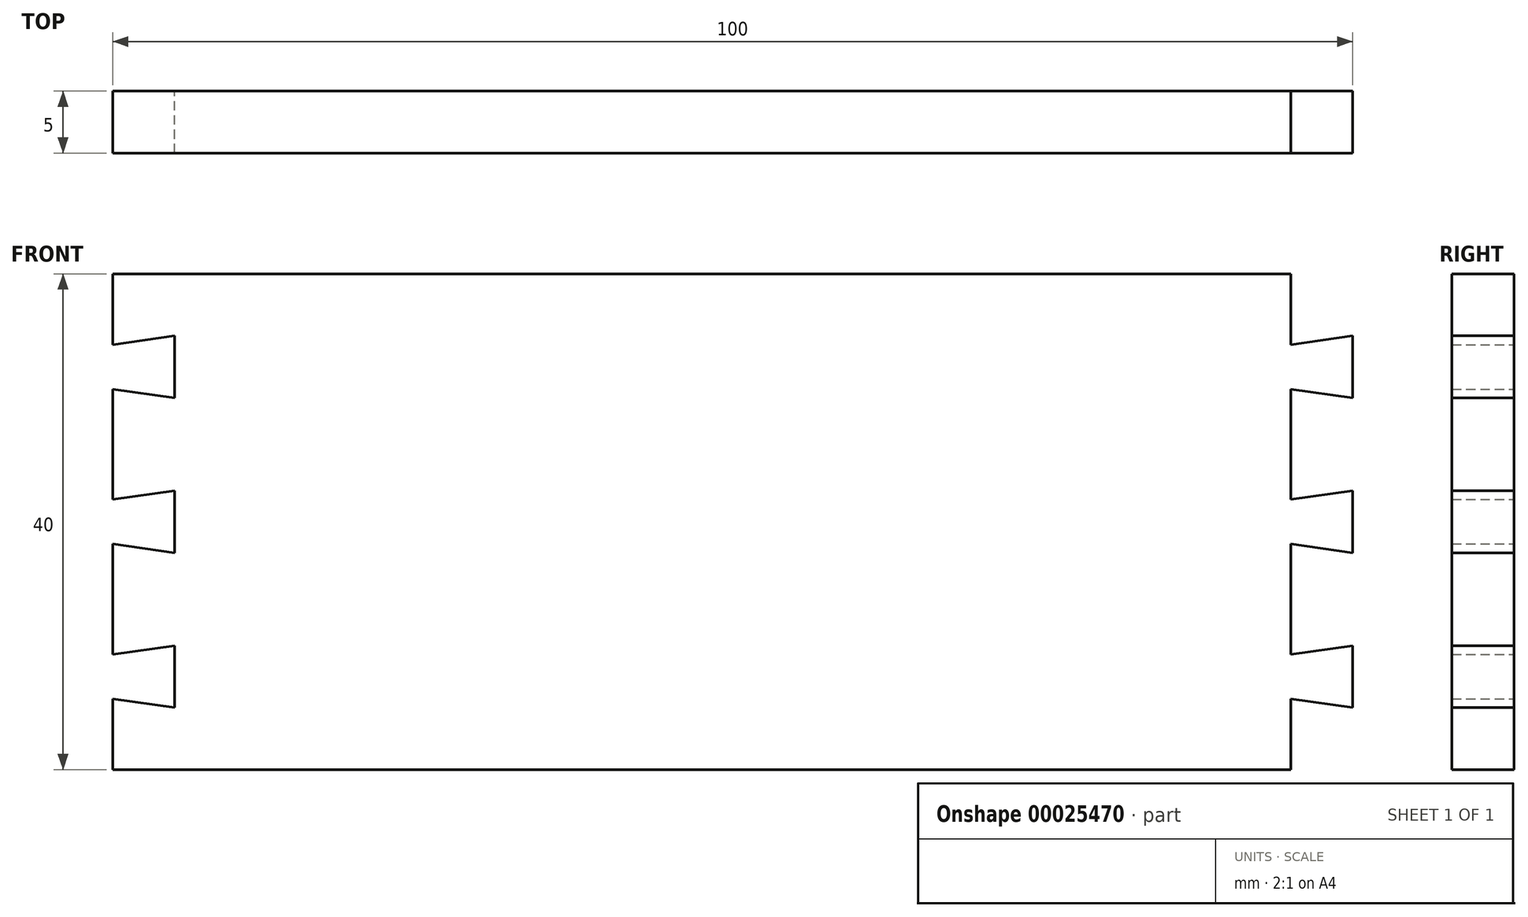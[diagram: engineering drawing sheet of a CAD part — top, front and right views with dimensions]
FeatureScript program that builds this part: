
annotation { "Feature Type Name" : "Feature", "Feature Type Description" : "" }
export const myFeature = defineFeature(function(context is Context, id is Id, definition is map)
    precondition{}
    {
        {
            var Q0;
            Q0=qCreatedBy(makeId("Front.planeOp"),FACE);
            var sketch = newSketch(context, id + "F0", { "sketchPlane" : qUnion([Q0])});
            skLineSegment(sketch, "E0.bottom", {"start": v(0, 0) * mm, "end": v(100, 0) * mm});
            skLineSegment(sketch, "E0.top", {"start": v(0, -40) * mm, "end": v(100, -40) * mm});
            skLineSegment(sketch, "E0.left", {"start": v(0, 0) * mm, "end": v(0, -5.7) * mm});
            skLineSegment(sketch, "E0.right", {"start": v(100, 0) * mm, "end": v(100, -40) * mm});
            skLineSegment(sketch, "E1", {"start": v(0, -5.7) * mm, "end": v(5, -5) * mm});
            skLineSegment(sketch, "E2", {"start": v(5, -5) * mm, "end": v(5, -10) * mm});
            skLineSegment(sketch, "E3", {"start": v(5, -10) * mm, "end": v(0, -9.3) * mm});
            skLineSegment(sketch, "E4.0.1.0", {"start": v(0, -18.2) * mm, "end": v(5, -17.5) * mm});
            skLineSegment(sketch, "E4.0.1.1", {"start": v(5, -17.5) * mm, "end": v(5, -22.5) * mm});
            skLineSegment(sketch, "E4.0.1.2", {"start": v(5, -22.5) * mm, "end": v(0, -21.8) * mm});
            skLineSegment(sketch, "E4.0.2.0", {"start": v(0, -30.7) * mm, "end": v(5, -30) * mm});
            skLineSegment(sketch, "E4.0.2.1", {"start": v(5, -30) * mm, "end": v(5, -35) * mm});
            skLineSegment(sketch, "E4.0.2.2", {"start": v(5, -35) * mm, "end": v(0, -34.3) * mm});
            skLineSegment(sketch, "E4.direction1", {"start": v(0, -5.7) * mm, "end": v(25, -5.7) * mm, "construction": true});
            skLineSegment(sketch, "E4.direction2", {"start": v(0, -5.7) * mm, "end": v(0, -18.2) * mm, "construction": true});
            skLineSegment(sketch, "E5", {"start": v(95, 19.16) * mm, "end": v(95, -53.98) * mm});
            skLineSegment(sketch, "E6", {"start": v(100, -5) * mm, "end": v(95, -5.7) * mm});
            skLineSegment(sketch, "E7", {"start": v(95, -5.7) * mm, "end": v(95, -9.3) * mm});
            skLineSegment(sketch, "E8", {"start": v(95, -9.3) * mm, "end": v(100, -10) * mm});
            skLineSegment(sketch, "E9", {"start": v(0, -5.7) * mm, "end": v(0, -9.3) * mm});
            skLineSegment(sketch, "E10", {"start": v(0, -9.3) * mm, "end": v(0, -40) * mm});
            skLineSegment(sketch, "E11.0.1.0", {"start": v(100, -17.5) * mm, "end": v(95, -18.2) * mm});
            skLineSegment(sketch, "E11.0.1.1", {"start": v(95, -21.8) * mm, "end": v(100, -22.5) * mm});
            skLineSegment(sketch, "E11.0.2.0", {"start": v(100, -30) * mm, "end": v(95, -30.7) * mm});
            skLineSegment(sketch, "E11.0.2.1", {"start": v(95, -34.3) * mm, "end": v(100, -35) * mm});
            skLineSegment(sketch, "E11.direction1", {"start": v(95, -5.7) * mm, "end": v(120, -5.7) * mm, "construction": true});
            skLineSegment(sketch, "E11.direction2", {"start": v(95, -5.7) * mm, "end": v(95, -18.2) * mm, "construction": true});
            skSolve(sketch);
        }
        {
            var Q0;
            {var subQ17=sQuery(id+"F0.wireOp",EDGE,"E0.left");Q0=makeQuery(id+"F0.imprint","IMPRINT",FACE,{"disambiguationData":[TD([[makeQuery(id+"F0.imprint","IMPRINT",EDGE,{"derivedFrom":subQ17}),1.0]])]});}
            var Q1;
            {var subQ1=sQuery(id+"F0.wireOp",EDGE,"E6");Q1=makeQuery(id+"F0.imprint","IMPRINT",FACE,{"disambiguationData":[TD([[makeQuery(id+"F0.imprint","IMPRINT",EDGE,{"derivedFrom":subQ1}),1.0]])]});}
            var Q2;
            {var subQ1=sQuery(id+"F0.wireOp",EDGE,"E11.0.1.0");Q2=makeQuery(id+"F0.imprint","IMPRINT",FACE,{"disambiguationData":[TD([[makeQuery(id+"F0.imprint","IMPRINT",EDGE,{"derivedFrom":subQ1}),1.0]])]});}
            var Q3;
            {var subQ1=sQuery(id+"F0.wireOp",EDGE,"E11.0.2.0");Q3=makeQuery(id+"F0.imprint","IMPRINT",FACE,{"disambiguationData":[TD([[makeQuery(id+"F0.imprint","IMPRINT",EDGE,{"derivedFrom":subQ1}),1.0]])]});}
            extrude(context, id + "F1", {"entities" : qUnion([Q0, Q1, Q2, Q3]), "depth" : 5 * mm, "symmetric" : true});
        }
    });
